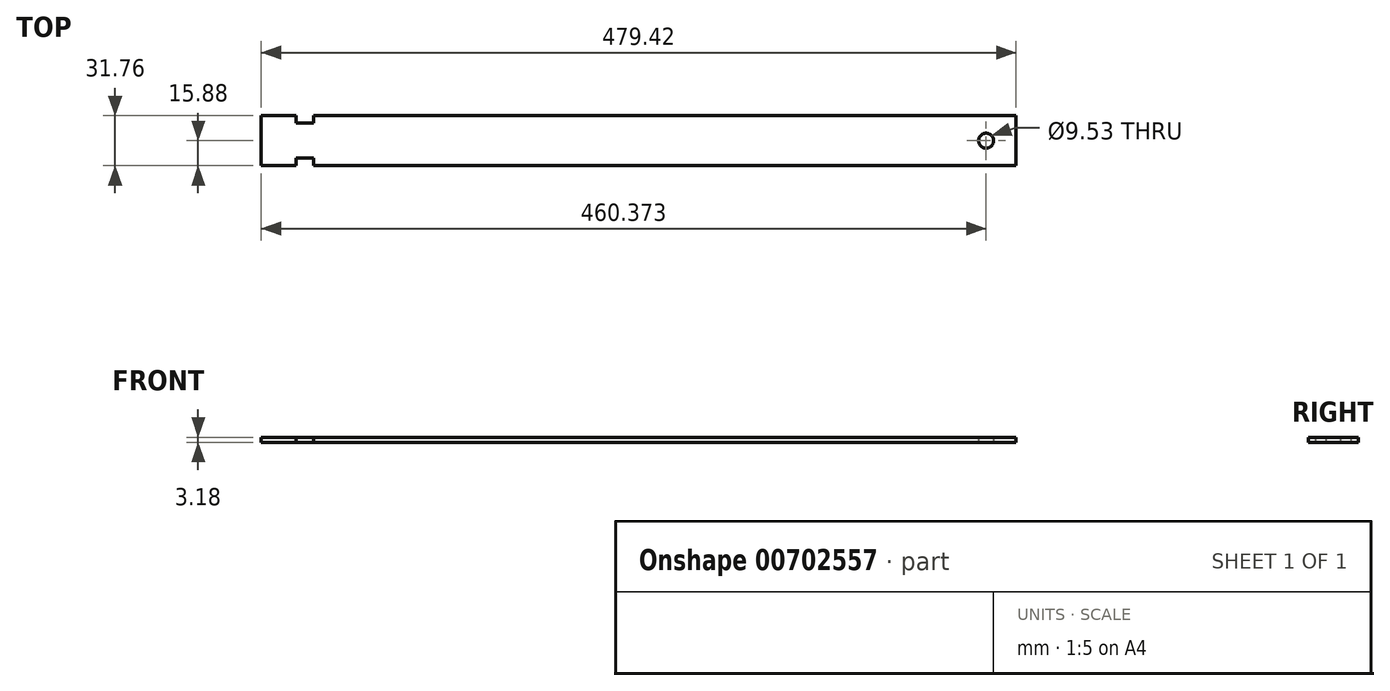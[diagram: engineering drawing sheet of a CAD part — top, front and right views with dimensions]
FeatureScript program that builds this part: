
annotation { "Feature Type Name" : "Feature", "Feature Type Description" : "" }
export const myFeature = defineFeature(function(context is Context, id is Id, definition is map)
    precondition{}
    {
        {
            var Q0;
            Q0=qCreatedBy(makeId("Top.planeOp"),FACE);
            var sketch = newSketch(context, id + "F0", { "sketchPlane" : qUnion([Q0])});
            skLineSegment(sketch, "E0.bottom", {"start": v(239.71, -15.87) * mm, "end": v(-239.71, -15.88) * mm});
            skLineSegment(sketch, "E0.top", {"start": v(239.71, 15.88) * mm, "end": v(-239.71, 15.87) * mm});
            skLineSegment(sketch, "E0.left", {"start": v(239.71, -15.87) * mm, "end": v(239.71, 15.88) * mm});
            skLineSegment(sketch, "E0.right", {"start": v(-239.71, -15.88) * mm, "end": v(-239.71, 15.87) * mm});
            skPoint(sketch, "E0.middle", {"position": v(0, 0) * mm});
            skLineSegment(sketch, "E1.bottom", {"start": v(-217.49, 15.87) * mm, "end": v(-206.38, 15.87) * mm});
            skLineSegment(sketch, "E1.top", {"start": v(-217.49, 11.11) * mm, "end": v(-206.38, 11.11) * mm});
            skLineSegment(sketch, "E1.left", {"start": v(-217.49, 15.87) * mm, "end": v(-217.49, 11.11) * mm});
            skLineSegment(sketch, "E1.right", {"start": v(-206.38, 15.87) * mm, "end": v(-206.38, 11.11) * mm});
            skLineSegment(sketch, "E2.MirrorCS", {"start": v(239.71, -15.88) * mm, "end": v(-239.71, -15.87) * mm});
            skLineSegment(sketch, "E3.MirrorCS", {"start": v(-217.49, -15.87) * mm, "end": v(-206.38, -15.87) * mm});
            skLineSegment(sketch, "E4.MirrorCS", {"start": v(-217.49, -11.11) * mm, "end": v(-206.38, -11.11) * mm});
            skLineSegment(sketch, "E5.MirrorCS", {"start": v(-206.38, -15.87) * mm, "end": v(-206.38, -11.11) * mm});
            skLineSegment(sketch, "E6.MirrorCS", {"start": v(-217.49, -15.87) * mm, "end": v(-217.49, -11.11) * mm});
            skCircle(sketch, "E7", {"center": v(220.66, 0) * mm, "radius": 4.76 * mm});
            skSolve(sketch);
        }
        {
            var Q0;
            {var subQ4=sQuery(id+"F0.wireOp",EDGE,"E0.left");Q0=makeQuery(id+"F0.imprint","IMPRINT",FACE,{"disambiguationData":[TD([[makeQuery(id+"F0.imprint","IMPRINT",EDGE,{"derivedFrom":subQ4}),1.0]])]});}
            extrude(context, id + "F1", {"entities" : qUnion([Q0]), "depth" : 3.17 * mm, "offsetDistance" : 25.4 * mm});
        }
    });
